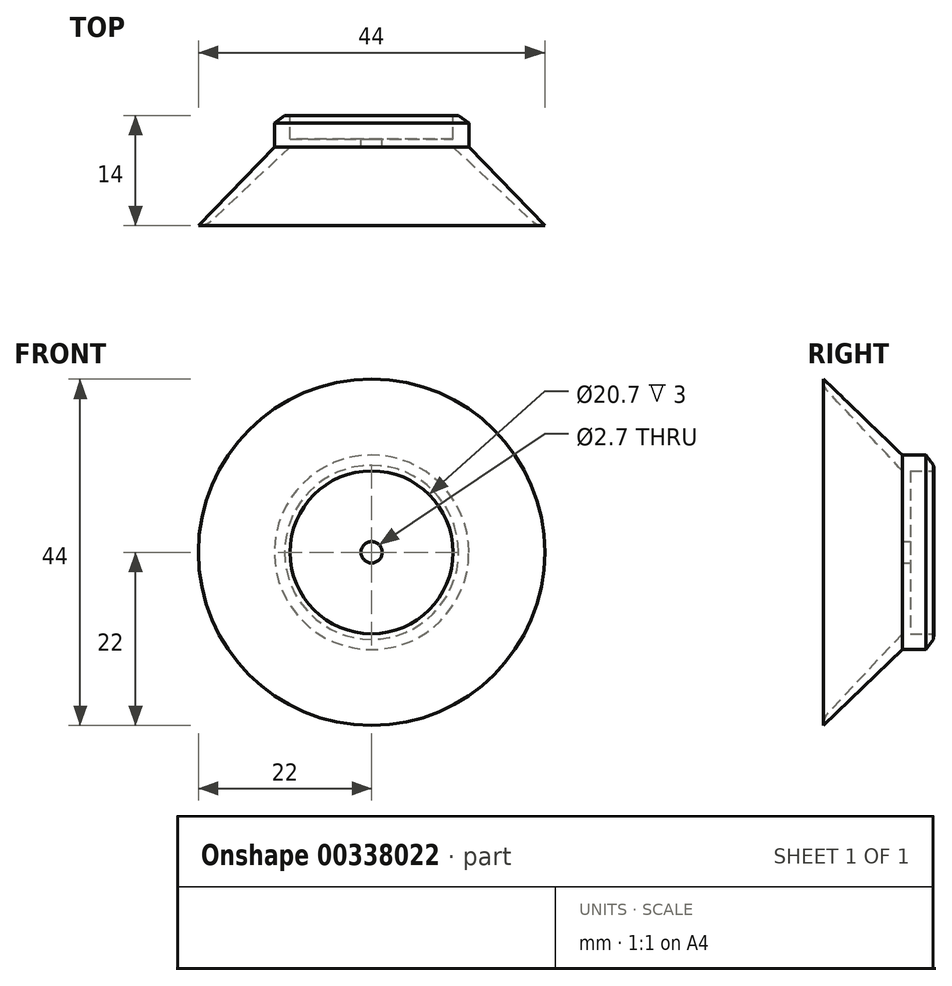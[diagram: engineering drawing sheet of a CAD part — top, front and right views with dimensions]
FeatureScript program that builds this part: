
annotation { "Feature Type Name" : "Feature", "Feature Type Description" : "" }
export const myFeature = defineFeature(function(context is Context, id is Id, definition is map)
    precondition{}
    {
        {
            var Q0;
            Q0=qCreatedBy(makeId("Top.planeOp"),FACE);
            var sketch = newSketch(context, id + "F0", { "sketchPlane" : qUnion([Q0])});
            skLineSegment(sketch, "E0", {"start": v(0, 0) * mm, "end": v(12.35, 0) * mm, "construction": true});
            skLineSegment(sketch, "E1", {"start": v(0, 0) * mm, "end": v(0, -10) * mm, "construction": true});
            skLineSegment(sketch, "E2", {"start": v(-21, -10) * mm, "end": v(-22, -10) * mm, "construction": true});
            skLineSegment(sketch, "E3", {"start": v(0, -10) * mm, "end": v(22, -10) * mm, "construction": true});
            skPoint(sketch, "E4", {"position": v(-11.57, 0) * mm});
            skPoint(sketch, "E5", {"position": v(10.62, 0) * mm});
            skLineSegment(sketch, "E6", {"start": v(12.35, 0) * mm, "end": v(22, -10) * mm});
            skLineSegment(sketch, "E7", {"start": v(12.35, 0) * mm, "end": v(10.35, 0) * mm});
            skLineSegment(sketch, "E8", {"start": v(-22, -10) * mm, "end": v(-21, -10) * mm});
            skLineSegment(sketch, "E9", {"start": v(22, -10) * mm, "end": v(21.8, -10) * mm});
            skLineSegment(sketch, "E10", {"start": v(20.42, -9.46) * mm, "end": v(10.35, 0) * mm});
            skLineSegment(sketch, "E11", {"start": v(10.35, 0) * mm, "end": v(2.04, 0) * mm});
            skLineSegment(sketch, "E12", {"start": v(10.35, 0) * mm, "end": v(10.35, 3) * mm});
            skLineSegment(sketch, "E13", {"start": v(10.35, 3) * mm, "end": v(12.35, 3) * mm});
            skLineSegment(sketch, "E14", {"start": v(12.35, 0) * mm, "end": v(12.35, 3) * mm});
            skPoint(sketch, "E15.visualSharp", {"position": v(21, -10) * mm});
            skArc(sketch, "E15.filletArc", {"start": v(20.42, -9.46) * mm, "mid": v(21.06, -9.86) * mm, "end": v(21.8, -10) * mm});
            skLineSegment(sketch, "E16", {"start": v(10.35, 0) * mm, "end": v(1.35, 0) * mm});
            skLineSegment(sketch, "E17", {"start": v(1.35, 0) * mm, "end": v(1.35, 1) * mm});
            skLineSegment(sketch, "E18", {"start": v(1.35, 1) * mm, "end": v(10.35, 1) * mm});
            skLineSegment(sketch, "E19", {"start": v(12.35, 3) * mm, "end": v(11.05, 3.97) * mm});
            skLineSegment(sketch, "E20", {"start": v(10.35, 3) * mm, "end": v(10.35, 4) * mm});
            skLineSegment(sketch, "E21", {"start": v(10.35, 4) * mm, "end": v(11.05, 3.97) * mm});
            skSolve(sketch);
        }
        {
            var Q0;
            Q0=makeQuery(id+"F0.imprint","IMPRINT",FACE,{"disambiguationData":[TD([[makeQuery(id+"F0.imprint","IMPRINT",EDGE,{"derivedFrom":sQuery(id+"F0.wireOp",EDGE,"E6")}),-1.0]])]});
            var Q1;
            {var subQ4=sQuery(id+"F0.wireOp",EDGE,"E17");Q1=makeQuery(id+"F0.imprint","IMPRINT",FACE,{"disambiguationData":[TD([[makeQuery(id+"F0.imprint","IMPRINT",EDGE,{"derivedFrom":subQ4}),-1.0]])]});}
            var Q2;
            {var subQ3=sQuery(id+"F0.wireOp",EDGE,"E7");Q2=makeQuery(id+"F0.imprint","IMPRINT",FACE,{"disambiguationData":[TD([[makeQuery(id+"F0.imprint","IMPRINT",EDGE,{"derivedFrom":subQ3}),-1.0]])]});}
            var Q3;
            Q3=makeQuery(id+"F0.imprint","IMPRINT",FACE,{"disambiguationData":[TD([[makeQuery(id+"F0.imprint","IMPRINT",EDGE,{"derivedFrom":sQuery(id+"F0.wireOp",EDGE,"E13")}),1.0]])]});
            var Q4;
            Q4=sQuery(id+"F0.wireOp",EDGE,"E1");
            revolve(context, id + "F1", {"entities" : qUnion([Q0, Q1, Q2, Q3]), "axis" : qUnion([Q4]), "revolveType" : RevolveType.FULL});
        }
    });
